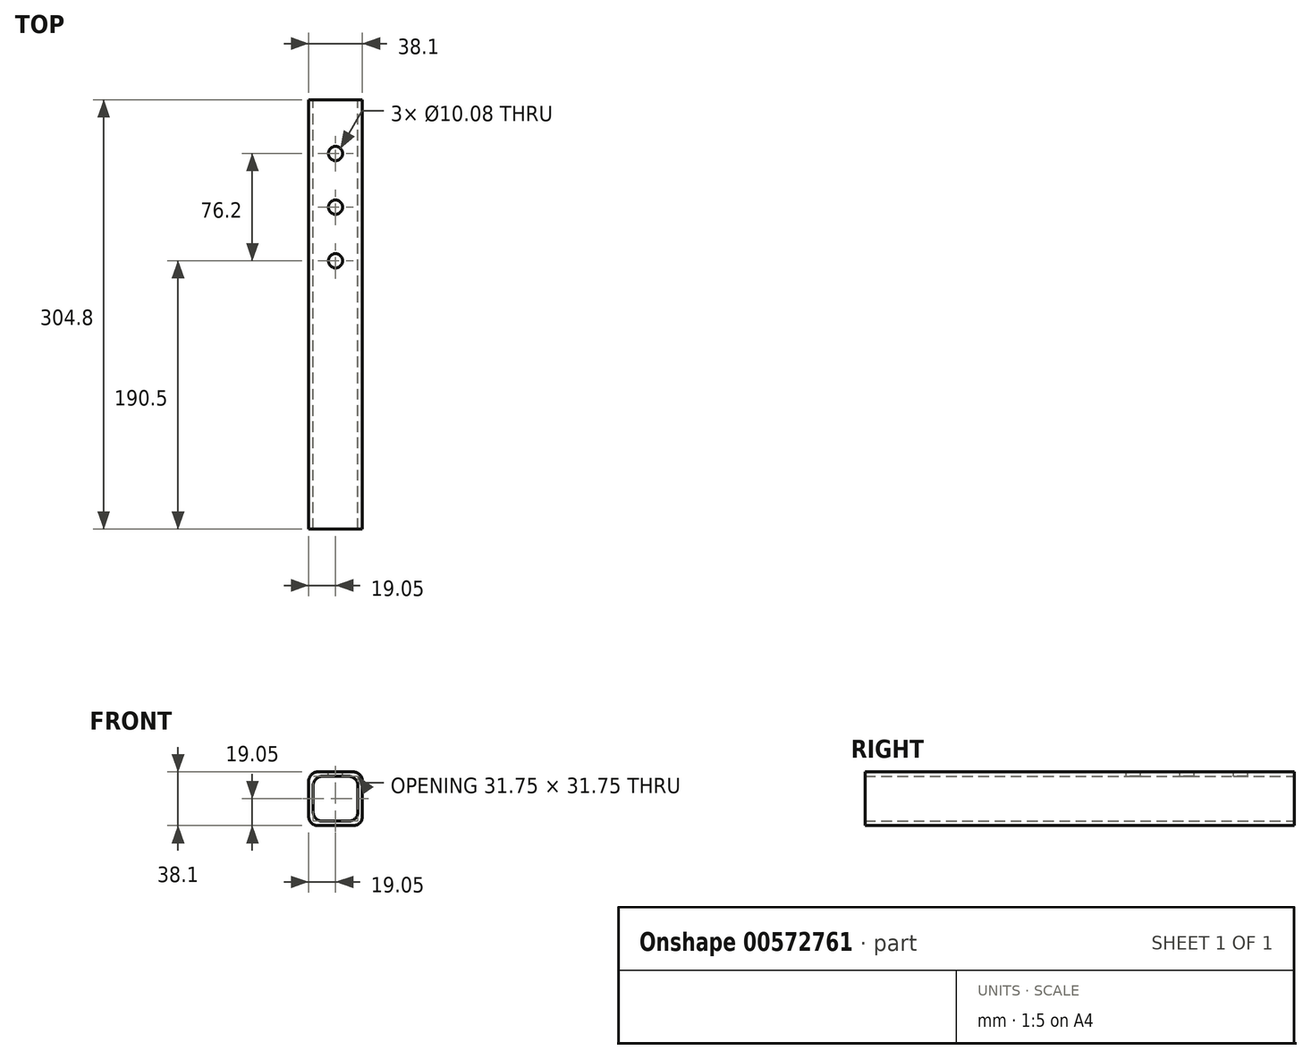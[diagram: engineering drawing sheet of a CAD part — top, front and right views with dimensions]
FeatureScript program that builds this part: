
annotation { "Feature Type Name" : "Feature", "Feature Type Description" : "" }
export const myFeature = defineFeature(function(context is Context, id is Id, definition is map)
    precondition{}
    {
        {
            var Q0;
            Q0=qCreatedBy(makeId("Front.planeOp"),FACE);
            var sketch = newSketch(context, id + "F0", { "sketchPlane" : qUnion([Q0])});
            skLineSegment(sketch, "E0.bottom", {"start": v(6.35, 0) * mm, "end": v(31.75, 0) * mm});
            skLineSegment(sketch, "E0.top", {"start": v(6.35, 38.1) * mm, "end": v(31.75, 38.1) * mm});
            skLineSegment(sketch, "E0.left", {"start": v(0, 6.35) * mm, "end": v(0, 31.75) * mm});
            skLineSegment(sketch, "E0.right", {"start": v(38.1, 6.35) * mm, "end": v(38.1, 31.75) * mm});
            skLineSegment(sketch, "E1.bottom", {"start": v(9.52, 3.18) * mm, "end": v(28.57, 3.18) * mm});
            skLineSegment(sketch, "E1.top", {"start": v(9.52, 34.92) * mm, "end": v(28.57, 34.92) * mm});
            skLineSegment(sketch, "E1.left", {"start": v(3.17, 9.52) * mm, "end": v(3.17, 28.57) * mm});
            skLineSegment(sketch, "E1.right", {"start": v(34.92, 9.53) * mm, "end": v(34.92, 28.57) * mm});
            skPoint(sketch, "E2.visualSharp", {"position": v(0, 38.1) * mm});
            skArc(sketch, "E2.filletArc", {"start": v(6.35, 38.1) * mm, "mid": v(1.86, 36.24) * mm, "end": v(0, 31.75) * mm});
            skPoint(sketch, "E3.visualSharp", {"position": v(34.92, 34.92) * mm});
            skArc(sketch, "E3.filletArc", {"start": v(34.92, 28.57) * mm, "mid": v(33.07, 33.07) * mm, "end": v(28.57, 34.92) * mm});
            skPoint(sketch, "E4.visualSharp", {"position": v(3.17, 34.92) * mm});
            skArc(sketch, "E4.filletArc", {"start": v(9.52, 34.92) * mm, "mid": v(5.03, 33.07) * mm, "end": v(3.17, 28.57) * mm});
            skPoint(sketch, "E5.visualSharp", {"position": v(38.1, 38.1) * mm});
            skArc(sketch, "E5.filletArc", {"start": v(38.1, 31.75) * mm, "mid": v(36.24, 36.24) * mm, "end": v(31.75, 38.1) * mm});
            skPoint(sketch, "E6.visualSharp", {"position": v(38.1, 0) * mm});
            skArc(sketch, "E6.filletArc", {"start": v(31.75, 0) * mm, "mid": v(36.24, 1.86) * mm, "end": v(38.1, 6.35) * mm});
            skPoint(sketch, "E7.visualSharp", {"position": v(0, 0) * mm});
            skArc(sketch, "E7.filletArc", {"start": v(0, 6.35) * mm, "mid": v(1.86, 1.86) * mm, "end": v(6.35, 0) * mm});
            skPoint(sketch, "E8.visualSharp", {"position": v(3.17, 3.18) * mm});
            skArc(sketch, "E8.filletArc", {"start": v(3.17, 9.52) * mm, "mid": v(5.03, 5.03) * mm, "end": v(9.52, 3.18) * mm});
            skPoint(sketch, "E9.visualSharp", {"position": v(34.92, 3.18) * mm});
            skArc(sketch, "E9.filletArc", {"start": v(28.57, 3.18) * mm, "mid": v(33.07, 5.03) * mm, "end": v(34.92, 9.53) * mm});
            skSolve(sketch);
        }
        {
            var Q0;
            Q0 = qSketchRegion(id + "F0", true);
            extrude(context, id + "F1", {"entities" : qUnion([Q0]), "depth" : 304.8 * mm, "offsetDistance" : 25.4 * mm});
        }
        {
            var Q0;
            Q0=makeQuery(id+"F1.opExtrude","SWEPT_FACE",FACE,{"disambiguationData":[OSD([sQuery(id+"F0.wireOp",EDGE,"E0.top")])]});
            var sketch = newSketch(context, id + "F2", { "sketchPlane" : qUnion([Q0])});
            skPoint(sketch, "E10", {"position": v(19.05, -38.1) * mm});
            skPoint(sketch, "E10.positionSnap0", {"position": v(19.05, 0) * mm});
            skPoint(sketch, "E11", {"position": v(19.05, -76.2) * mm});
            skPoint(sketch, "E12", {"position": v(19.05, -114.3) * mm});
            skSolve(sketch);
        }
        {
            var Q0;
            Q0=sQuery(id+"F2.wireOp",VERTEX,"E10");
            var Q1;
            Q1=sQuery(id+"F2.wireOp",VERTEX,"E11");
            var Q2;
            Q2=sQuery(id+"F2.wireOp",VERTEX,"E12");
            var Q3;
            Q3=makeQuery(id+"F1.opExtrude","SWEPT_BODY",BODY,{"disambiguationData":[OSD([sQuery(id+"F0.wireOp",EDGE,"E0.bottom"),sQuery(id+"F0.wireOp",EDGE,"E0.top"),sQuery(id+"F0.wireOp",EDGE,"E0.left"),sQuery(id+"F0.wireOp",EDGE,"E0.right"),sQuery(id+"F0.wireOp",EDGE,"E1.bottom"),sQuery(id+"F0.wireOp",EDGE,"E1.top"),sQuery(id+"F0.wireOp",EDGE,"E1.left"),sQuery(id+"F0.wireOp",EDGE,"E1.right"),sQuery(id+"F0.wireOp",EDGE,"E2.filletArc"),sQuery(id+"F0.wireOp",EDGE,"E3.filletArc"),sQuery(id+"F0.wireOp",EDGE,"E4.filletArc"),sQuery(id+"F0.wireOp",EDGE,"E5.filletArc"),sQuery(id+"F0.wireOp",EDGE,"E6.filletArc"),sQuery(id+"F0.wireOp",EDGE,"E7.filletArc"),sQuery(id+"F0.wireOp",EDGE,"E8.filletArc"),sQuery(id+"F0.wireOp",EDGE,"E9.filletArc")])]});
            hole(context, id + "F3", {"style" : HoleStyle.SIMPLE, "endStyle" : HoleEndStyle.BLIND, "standardTappedOrClearance" : lookupTablePath({ "standard" : "ANSI", "fit" : "Normal (ASME)", "size" : "3/8", "type" : "Clearance" }), "standardBlindInLast" : lookupTablePath({ "fit" : "Free", "standard" : "ANSI", "size" : "3/8", "type" : "Clearance" }), "holeDiameter" : 10.08 * mm, "holeDepth" : 12.7 * mm, "tappedDepth" : 20.65 * mm, "tapClearance" : 3, "startFromSketch" : true, "locations" : qUnion([Q0, Q1, Q2]), "scope" : qUnion([Q3])});
        }
    });
